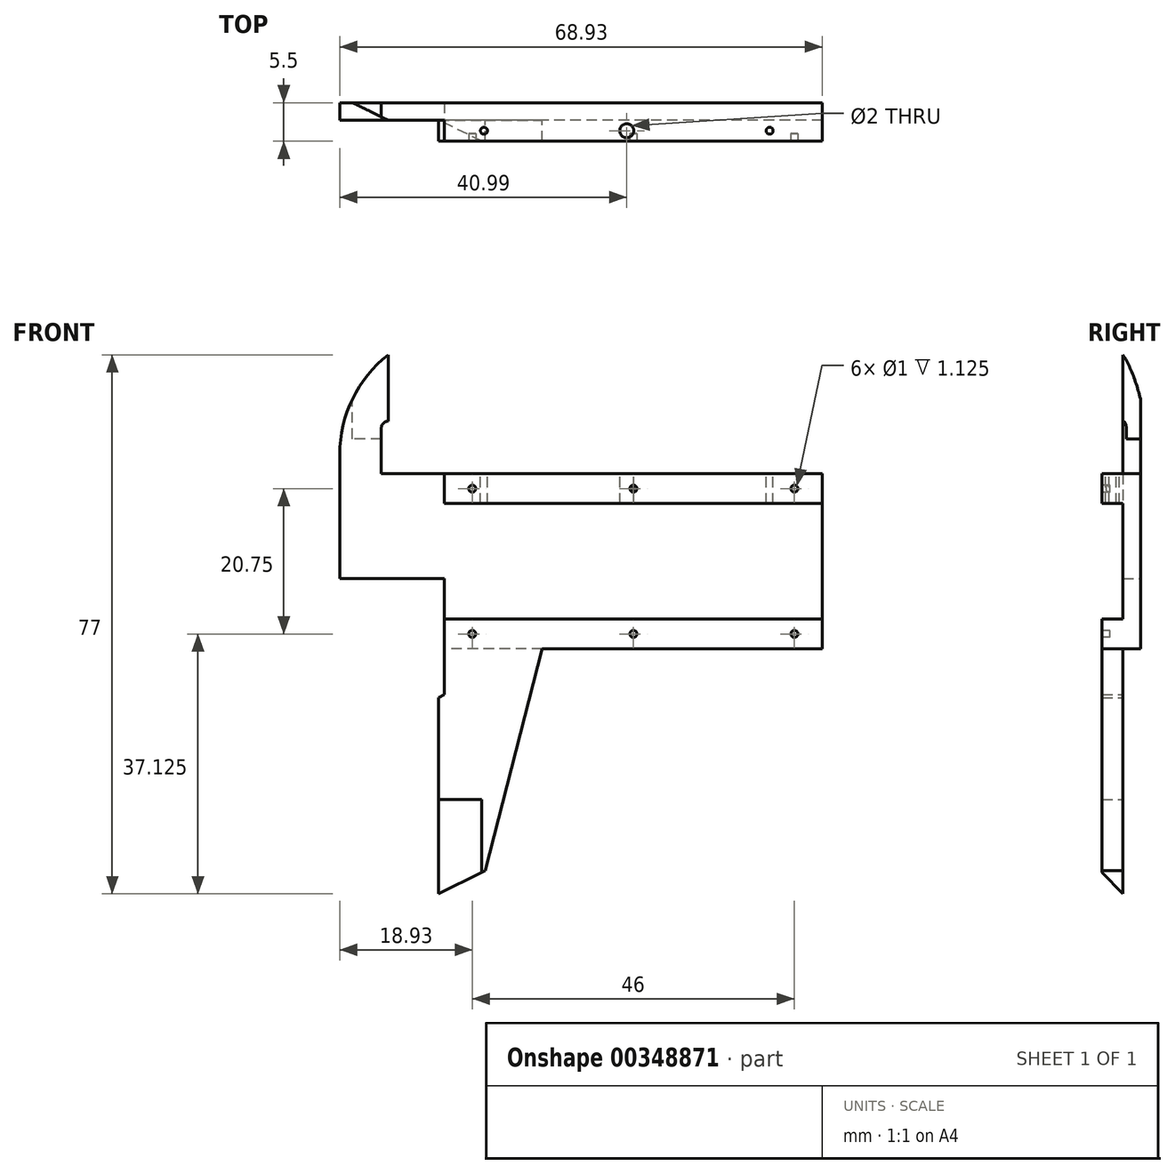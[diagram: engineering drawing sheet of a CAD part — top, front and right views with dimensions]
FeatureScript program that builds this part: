
annotation { "Feature Type Name" : "Feature", "Feature Type Description" : "" }
export const myFeature = defineFeature(function(context is Context, id is Id, definition is map)
    precondition{}
    {
        {
            var Q0;
            Q0=qCreatedBy(makeId("Front.planeOp"),FACE);
            var sketch = newSketch(context, id + "F0", { "sketchPlane" : qUnion([Q0])});
            skLineSegment(sketch, "E0", {"start": v(0, 0) * mm, "end": v(-55.4, 0) * mm, "construction": true});
            skLineSegment(sketch, "E1", {"start": v(0, 12.5) * mm, "end": v(0, -12.5) * mm});
            skLineSegment(sketch, "E2", {"start": v(0, -12.5) * mm, "end": v(-40, -12.5) * mm});
            skLineSegment(sketch, "E3", {"start": v(-40, -12.5) * mm, "end": v(-48.17, -44.18) * mm});
            skLineSegment(sketch, "E4", {"start": v(-48.17, -44.18) * mm, "end": v(-54.8, -47.5) * mm});
            skLineSegment(sketch, "E5", {"start": v(-54.8, -47.5) * mm, "end": v(-54.8, -19.5) * mm});
            skLineSegment(sketch, "E6", {"start": v(-54.8, -19.5) * mm, "end": v(-54, -19.04) * mm});
            skLineSegment(sketch, "E7", {"start": v(-54, -19.04) * mm, "end": v(-54, -2.5) * mm});
            skLineSegment(sketch, "E8", {"start": v(-54, -2.5) * mm, "end": v(-68.93, -2.5) * mm});
            skLineSegment(sketch, "E9", {"start": v(-68.93, -2.5) * mm, "end": v(-68.93, 15.3) * mm});
            skLineSegment(sketch, "E10", {"start": v(0, 12.5) * mm, "end": v(-63, 12.5) * mm});
            skLineSegment(sketch, "E11", {"start": v(-63, 12.5) * mm, "end": v(-63, 19) * mm});
            skLineSegment(sketch, "E12", {"start": v(-62, 20) * mm, "end": v(-62, 29.5) * mm});
            skArc(sketch, "E13", {"start": v(-62, 29.5) * mm, "mid": v(-67.1, 23.2) * mm, "end": v(-68.93, 15.3) * mm});
            skArc(sketch, "E14", {"start": v(-62, 20) * mm, "mid": v(-62.7, 19.7) * mm, "end": v(-63, 19) * mm});
            skSolve(sketch);
        }
        {
            var Q0;
            Q0=qSketchRegion(id+"F0",true);
            extrude(context, id + "F1", {"entities" : qUnion([Q0]), "depth" : 5.5 * mm});
        }
        {
            var Q0;
            Q0=makeQuery(id+"F1.opExtrude","CAP_FACE",FACE,{"disambiguationData":[OSD([sQuery(id+"F0.wireOp",EDGE,"E1"),sQuery(id+"F0.wireOp",EDGE,"E2"),sQuery(id+"F0.wireOp",EDGE,"E3"),sQuery(id+"F0.wireOp",EDGE,"E4"),sQuery(id+"F0.wireOp",EDGE,"E5"),sQuery(id+"F0.wireOp",EDGE,"E6"),sQuery(id+"F0.wireOp",EDGE,"E7"),sQuery(id+"F0.wireOp",EDGE,"E8"),sQuery(id+"F0.wireOp",EDGE,"E9"),sQuery(id+"F0.wireOp",EDGE,"E10"),sQuery(id+"F0.wireOp",EDGE,"E11"),sQuery(id+"F0.wireOp",EDGE,"E12"),sQuery(id+"F0.wireOp",EDGE,"E13"),sQuery(id+"F0.wireOp",EDGE,"E14")])],"isStart":false});
            var sketch = newSketch(context, id + "F2", { "sketchPlane" : qUnion([Q0])});
            skLineSegment(sketch, "E15", {"start": v(0, 8.25) * mm, "end": v(0, -8.25) * mm});
            skLineSegment(sketch, "E16", {"start": v(0, -8.25) * mm, "end": v(-54, -8.25) * mm});
            skLineSegment(sketch, "E17", {"start": v(-54, -8.25) * mm, "end": v(-54, -2.5) * mm});
            skLineSegment(sketch, "E18", {"start": v(-54, -2.5) * mm, "end": v(-73.78, -2.5) * mm});
            skLineSegment(sketch, "E19", {"start": v(-73.78, -2.5) * mm, "end": v(-73.78, 31.93) * mm});
            skLineSegment(sketch, "E20", {"start": v(-73.78, 31.93) * mm, "end": v(-54, 31.93) * mm});
            skLineSegment(sketch, "E21", {"start": v(-54, 31.93) * mm, "end": v(-54, 8.25) * mm});
            skLineSegment(sketch, "E22", {"start": v(-54, 8.25) * mm, "end": v(0, 8.25) * mm});
            skSolve(sketch);
        }
        {
            var Q0;
            Q0=qSketchRegion(id+"F2",true);
            extrude(context, id + "F3", {"entities" : qUnion([Q0]), "operationType" : NewBodyOperationType.REMOVE, "oppositeDirection" : true, "depth" : 3 * mm});
        }
        {
            var Q0;
            {var subQ0=sQuery(id+"F0.wireOp",EDGE,"E1");var subQ1=sQuery(id+"F0.wireOp",EDGE,"E10");Q0=makeQuery(id+"F3.boolean.opBoolean","SPLIT",FACE,{"disambiguationData":[TD([makeQuery(id+"F1.opExtrude","SWEPT_FACE",FACE,{"disambiguationData":[OSD([subQ1])]})])],"derivedFrom":makeQuery(id+"F1.opExtrude","CAP_FACE",FACE,{"disambiguationData":[OSD([subQ0,sQuery(id+"F0.wireOp",EDGE,"E2"),sQuery(id+"F0.wireOp",EDGE,"E3"),sQuery(id+"F0.wireOp",EDGE,"E4"),sQuery(id+"F0.wireOp",EDGE,"E5"),sQuery(id+"F0.wireOp",EDGE,"E6"),sQuery(id+"F0.wireOp",EDGE,"E7"),sQuery(id+"F0.wireOp",EDGE,"E8"),sQuery(id+"F0.wireOp",EDGE,"E9"),subQ1,sQuery(id+"F0.wireOp",EDGE,"E11"),sQuery(id+"F0.wireOp",EDGE,"E12"),sQuery(id+"F0.wireOp",EDGE,"E13"),sQuery(id+"F0.wireOp",EDGE,"E14")])],"isStart":false})});}
            var sketch = newSketch(context, id + "F4", { "sketchPlane" : qUnion([Q0])});
            skLineSegment(sketch, "E23", {"start": v(0, 0) * mm, "end": v(-25.2, 0) * mm, "construction": true});
            skCircle(sketch, "E24", {"center": v(-4, 10.38) * mm, "radius": 0.5 * mm});
            skCircle(sketch, "E25", {"center": v(-27, 10.38) * mm, "radius": 0.5 * mm});
            skCircle(sketch, "E26", {"center": v(-50, 10.37) * mm, "radius": 0.5 * mm});
            skCircle(sketch, "E27.MirrorC", {"center": v(-50, -10.38) * mm, "radius": 0.5 * mm});
            skCircle(sketch, "E28.MirrorC", {"center": v(-27, -10.38) * mm, "radius": 0.5 * mm});
            skCircle(sketch, "E29.MirrorC", {"center": v(-4, -10.38) * mm, "radius": 0.5 * mm});
            skSolve(sketch);
        }
        {
            var Q0;
            Q0=qSketchRegion(id+"F4",true);
            extrude(context, id + "F5", {"entities" : qUnion([Q0]), "operationType" : NewBodyOperationType.REMOVE, "oppositeDirection" : true, "depth" : 1.12 * mm});
        }
        {
            var Q0;
            Q0=makeQuery(id+"F1.opExtrude","SWEPT_FACE",FACE,{"disambiguationData":[OSD([sQuery(id+"F0.wireOp",EDGE,"E10")])]});
            cPlane(context, id + "F6", {"entities" : qUnion([Q0]), "cplaneType" : CPlaneType.OFFSET, "offset" : 17.5 * mm, "width" : 150 * mm, "height" : 150 * mm});
        }
        {
            var Q0;
            Q0=makeQuery(id+"F1.opExtrude","SWEPT_FACE",FACE,{"disambiguationData":[OSD([sQuery(id+"F0.wireOp",EDGE,"E2")])]});
            var Q1;
            Q1=makeQuery(id+"F1.opExtrude","CAP_VERTEX",VERTEX,{"disambiguationData":[OSD([sQuery(id+"F0.wireOp",EDGE,"E4"),sQuery(id+"F0.wireOp",EDGE,"E5")])],"isStart":false});
            cPlane(context, id + "F7", {"entities" : qUnion([Q0, Q1]), "cplaneType" : CPlaneType.PLANE_POINT, "offset" : 34.75 * mm, "width" : 150 * mm, "height" : 150 * mm});
        }
        {
            var Q0;
            Q0=qCreatedBy(id+"F6.planeOp",FACE);
            var sketch = newSketch(context, id + "F8", { "sketchPlane" : qUnion([Q0])});
            skLineSegment(sketch, "E30.0", {"start": v(-62, -2.5) * mm, "end": v(-62, 0) * mm});
            skLineSegment(sketch, "E31", {"start": v(-62, 0) * mm, "end": v(-67.13, 0) * mm});
            skLineSegment(sketch, "E32", {"start": v(-67.13, 0) * mm, "end": v(-62, -2.5) * mm});
            skLineSegment(sketch, "E33", {"start": v(-62, -1.25) * mm, "end": v(-70.99, -1.25) * mm, "construction": true});
            skLineSegment(sketch, "E34.MirrorCS", {"start": v(-62, 0) * mm, "end": v(-62, -2.5) * mm});
            skSolve(sketch);
        }
        {
            var Q0;
            Q0=qSketchRegion(id+"F8",true);
            extrude(context, id + "F9", {"entities" : qUnion([Q0]), "operationType" : NewBodyOperationType.REMOVE, "oppositeDirection" : true, "depth" : 12.5 * mm});
        }
        {
            var Q0;
            Q0=makeQuery(id+"F1.opExtrude","SWEPT_FACE",FACE,{"disambiguationData":[OSD([sQuery(id+"F0.wireOp",EDGE,"E2")])]});
            var sketch = newSketch(context, id + "F10", { "sketchPlane" : qUnion([Q0])});
            skLineSegment(sketch, "E35.bottom", {"start": v(-40, 0) * mm, "end": v(-54.8, 0) * mm});
            skLineSegment(sketch, "E35.top", {"start": v(-40, 2.5) * mm, "end": v(-54.8, 2.5) * mm});
            skLineSegment(sketch, "E35.left", {"start": v(-40, 0) * mm, "end": v(-40, 2.5) * mm});
            skLineSegment(sketch, "E35.right", {"start": v(-54.8, 0) * mm, "end": v(-54.8, 2.5) * mm});
            skSolve(sketch);
        }
        {
            var Q0;
            Q0=qSketchRegion(id+"F10",true);
            extrude(context, id + "F11", {"entities" : qUnion([Q0]), "operationType" : NewBodyOperationType.REMOVE, "depth" : 47 * mm});
        }
        {
            var Q0;
            Q0=qCreatedBy(id+"F7.planeOp",FACE);
            var sketch = newSketch(context, id + "F12", { "sketchPlane" : qUnion([Q0])});
            skLineSegment(sketch, "E36.0", {"start": v(-54.8, 5.5) * mm, "end": v(-54.8, 2.5) * mm});
            skLineSegment(sketch, "E37", {"start": v(-54.8, 5.5) * mm, "end": v(-48.65, 5.5) * mm});
            skLineSegment(sketch, "E38", {"start": v(-48.65, 5.5) * mm, "end": v(-54.8, 2.5) * mm});
            skSolve(sketch);
        }
        {
            var Q0;
            Q0=qSketchRegion(id+"F12",true);
            extrude(context, id + "F13", {"entities" : qUnion([Q0]), "operationType" : NewBodyOperationType.REMOVE, "oppositeDirection" : true, "depth" : 13.5 * mm});
        }
        {
            var Q0;
            Q0=makeQuery(id+"F1.opExtrude","SWEPT_FACE",FACE,{"disambiguationData":[OSD([sQuery(id+"F0.wireOp",EDGE,"E10")])]});
            var sketch = newSketch(context, id + "F14", { "sketchPlane" : qUnion([Q0])});
            skCircle(sketch, "E39", {"center": v(-7.54, -4) * mm, "radius": 0.5 * mm});
            skCircle(sketch, "E40", {"center": v(-48.34, -4) * mm, "radius": 0.5 * mm});
            skSolve(sketch);
        }
        {
            var Q0;
            Q0=qSketchRegion(id+"F14",true);
            extrude(context, id + "F15", {"entities" : qUnion([Q0]), "operationType" : NewBodyOperationType.REMOVE, "endBound" : BoundingType.UP_TO_NEXT, "oppositeDirection" : true, "depth" : 3 * mm});
        }
        {
            var Q0;
            Q0=makeQuery(id+"F1.opExtrude","SWEPT_FACE",FACE,{"disambiguationData":[OSD([sQuery(id+"F0.wireOp",EDGE,"E10")])]});
            var sketch = newSketch(context, id + "F16", { "sketchPlane" : qUnion([Q0])});
            skCircle(sketch, "E41", {"center": v(-27.94, -4) * mm, "radius": 1 * mm});
            skPoint(sketch, "E42", {"position": v(-7.54, -4) * mm});
            skSolve(sketch);
        }
        {
            var Q0;
            Q0=qSketchRegion(id+"F16",true);
            extrude(context, id + "F17", {"entities" : qUnion([Q0]), "operationType" : NewBodyOperationType.REMOVE, "endBound" : BoundingType.UP_TO_NEXT, "oppositeDirection" : true, "depth" : 25 * mm});
        }
    });
